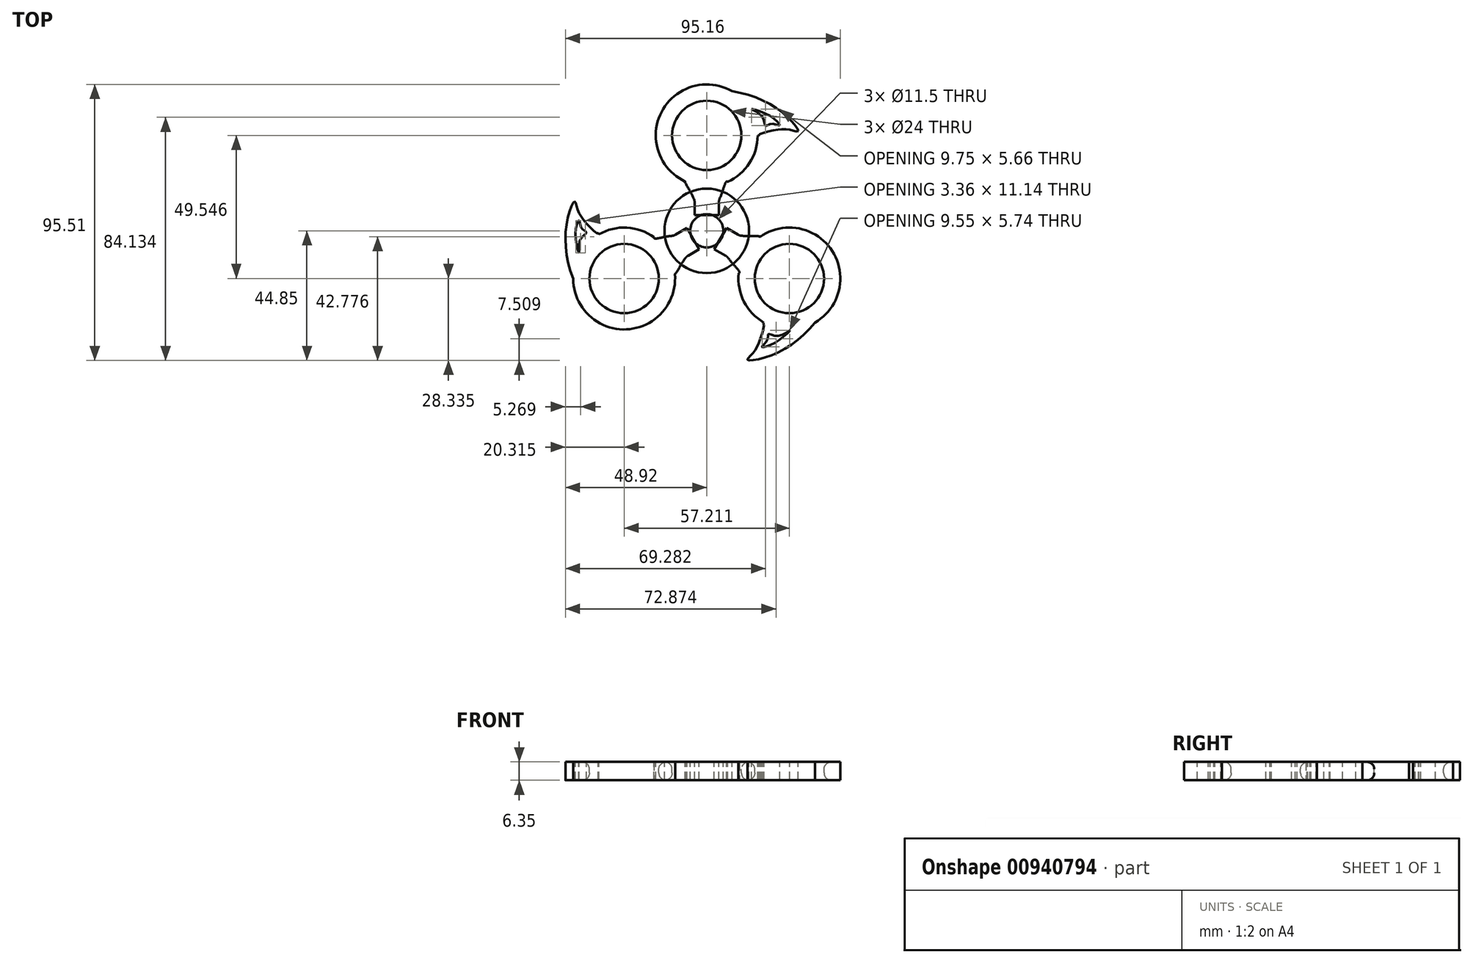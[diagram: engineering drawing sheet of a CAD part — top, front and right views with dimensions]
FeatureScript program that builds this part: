
annotation { "Feature Type Name" : "Feature", "Feature Type Description" : "" }
export const myFeature = defineFeature(function(context is Context, id is Id, definition is map)
    precondition{}
    {
        {
            var Q0;
            Q0=qCreatedBy(makeId("Top.planeOp"),FACE);
            var sketch = newSketch(context, id + "F0", { "sketchPlane" : qUnion([Q0])});
            skCircle(sketch, "E0", {"center": v(0, 0) * mm, "radius": 14.63 * mm});
            skCircle(sketch, "E1", {"center": v(0, 0) * mm, "radius": 5.75 * mm});
            skSolve(sketch);
        }
        {
            var Q0;
            Q0=qCreatedBy(makeId("Top.planeOp"),FACE);
            var sketch = newSketch(context, id + "F1", { "sketchPlane" : qUnion([Q0])});
            skCircle(sketch, "E2", {"center": v(0, 33.03) * mm, "radius": 17.63 * mm});
            skLineSegment(sketch, "E3", {"start": v(0, 0) * mm, "end": v(0, 33.03) * mm});
            skLineSegment(sketch, "E4", {"start": v(4.23, 5.44) * mm, "end": v(4.23, 10.03) * mm});
            skFitSpline(sketch, "E5", {"points": [v(4.23, 10.68) * mm, v(5.48, 13.75) * mm, v(6.36, 16.35) * mm, v(7.2, 16.93) * mm], "startDerivative": vector(2.65, 5.53) * mm, "endDerivative": vector(4.3, -5.28) * mm});
            skLineSegment(sketch, "E6.MirrorCS", {"start": v(-4.23, 5.44) * mm, "end": v(-4.23, 9.98) * mm});
            skPoint(sketch, "E7.orphan", {"position": v(4.23, 15.91) * mm});
            skFitSpline(sketch, "E8", {"points": [v(-4.23, 10.68) * mm, v(-5.95, 13.99) * mm, v(-7.53, 16.96) * mm, v(-7.4, 16.89) * mm], "startDerivative": vector(-3.15, 6.3) * mm, "endDerivative": vector(4.2, -6.48) * mm});
            skPoint(sketch, "E9.trimOffspring.end.orphan", {"position": v(-4.23, 15.91) * mm});
            skCircle(sketch, "E10", {"center": v(0, 33.03) * mm, "radius": 12 * mm});
            skArc(sketch, "E11.filletArc", {"start": v(-4.23, 9.98) * mm, "mid": v(-4.3, 10.66) * mm, "end": v(-4.54, 11.3) * mm});
            skArc(sketch, "E12.filletArc", {"start": v(4.49, 11.24) * mm, "mid": v(4.3, 10.65) * mm, "end": v(4.23, 10.03) * mm});
            skLineSegment(sketch, "E13", {"start": v(-4.23, 5.44) * mm, "end": v(4.23, 5.44) * mm});
            skPoint(sketch, "E14.oppositeSnap0", {"position": v(4.23, 7.74) * mm});
            skFitSpline(sketch, "E15", {"points": [v(15.49, 42.12) * mm, v(19.16, 39.55) * mm, v(20.33, 36.37) * mm, v(22.34, 37.04) * mm, v(25.18, 36.54) * mm, v(22, 39.72) * mm, v(15.49, 42.12) * mm]});
            skLineSegment(sketch, "E16", {"start": v(-7.4, 16.89) * mm, "end": v(-7.45, 17.05) * mm});
            skFitSpline(sketch, "E17", {"points": [v(6.04, 48.65) * mm, v(26.25, 40.87) * mm, v(31.56, 34.5) * mm, v(28.73, 35.02) * mm, v(22.7, 34.66) * mm, v(18.06, 32.99) * mm, v(20.32, 32.14) * mm], "startDerivative": vector(79.19, -6.9) * mm, "endDerivative": vector(8.4, -3.4) * mm});
            skLineSegment(sketch, "E18", {"start": v(18.06, 32.99) * mm, "end": v(17.63, 32.99) * mm});
            skSolve(sketch);
        }
        {
            var Q0;
            Q0=makeQuery(id+"F0.imprint","IMPRINT",FACE,{"disambiguationData":[TD([[makeQuery(id+"F0.imprint","IMPRINT",EDGE,{"derivedFrom":sQuery(id+"F0.wireOp",EDGE,"E0")}),1.0]])]});
            var Q1;
            {var subQ0=sQuery(id+"F1.wireOp",EDGE,"E6.MirrorCS");Q1=makeQuery(id+"F1.imprint","IMPRINT",FACE,{"disambiguationData":[TD([[makeQuery(id+"F1.imprint","IMPRINT",EDGE,{"derivedFrom":subQ0}),-1.0]])]});}
            var Q2;
            {var subQ4=sQuery(id+"F1.wireOp",EDGE,"E4");Q2=makeQuery(id+"F1.imprint","IMPRINT",FACE,{"disambiguationData":[TD([[makeQuery(id+"F1.imprint","IMPRINT",EDGE,{"derivedFrom":subQ4}),1.0]])]});}
            var Q3;
            Q3=makeQuery(id+"F1.imprint","IMPRINT",FACE,{"disambiguationData":[TD([[makeQuery(id+"F1.imprint","IMPRINT",EDGE,{"derivedFrom":sQuery(id+"F1.wireOp",EDGE,"E10")}),-1.0]])]});
            var Q4;
            {var subQ0=sQuery(id+"F1.wireOp",EDGE,"0489ace8-70b7-4bd0-9044-f4604df46fbd");var subQ1=sQuery(id+"F1.wireOp",EDGE,"E2");var subQ2=makeQuery(id+"F1.imprint","INTERSECT",VERTEX,{"disambiguationData":[OD(1.0)],"derivedFrom":[subQ1,subQ0]});Q4=makeQuery(id+"F1.imprint","IMPRINT",FACE,{"disambiguationData":[TD([[makeQuery(id+"F1.imprint","IMPRINT",EDGE,{"disambiguationData":[TD([[subQ2,1.0]])],"derivedFrom":subQ1}),-1.0]])]});}
            var Q5;
            Q5=makeQuery(id+"F1.imprint","IMPRINT",FACE,{"disambiguationData":[TD([[makeQuery(id+"F1.imprint","IMPRINT",EDGE,{"derivedFrom":sQuery(id+"F1.wireOp",EDGE,"E15")}),-1.0]])]});
            extrude(context, id + "F2", {"entities" : qUnion([Q0, Q1, Q2, Q3, Q4, Q5]), "oppositeDirection" : true, "depth" : 6.35 * mm, "offsetDistance" : 25.4 * mm});
        }
        {
            var Q0;
            Q0=makeQuery(id+"F2.opExtrude","CAP_EDGE",EDGE,{"disambiguationData":[OSD([sQuery(id+"F1.wireOp",EDGE,"E10")])],"isStart":true});
            fillet(context, id + "F3", {"entities" : qUnion([Q0]), "radius" : 2.54 * mm, "tangentPropagation" : true, "allowEdgeOverflow" : false});
        }
        {
            var Q0;
            Q0=makeQuery(id+"F2.opExtrude","CAP_EDGE",EDGE,{"disambiguationData":[OSD([sQuery(id+"F1.wireOp",EDGE,"E10")])],"isStart":false});
            fillet(context, id + "F4", {"entities" : qUnion([Q0]), "radius" : 2.54 * mm, "tangentPropagation" : true, "allowEdgeOverflow" : false});
        }
        {
            var Q0;
            Q0=makeQuery(id+"F2.opExtrude","SWEPT_BODY",BODY,{"disambiguationData":[OSD([sQuery(id+"F1.wireOp",EDGE,"E2"),sQuery(id+"F1.wireOp",EDGE,"E4"),sQuery(id+"F1.wireOp",EDGE,"E5"),sQuery(id+"F1.wireOp",EDGE,"E6.MirrorCS"),sQuery(id+"F1.wireOp",EDGE,"E8"),sQuery(id+"F1.wireOp",EDGE,"E10"),sQuery(id+"F1.wireOp",EDGE,"E11.filletArc"),sQuery(id+"F1.wireOp",EDGE,"E12.filletArc"),sQuery(id+"F1.wireOp",EDGE,"E13")])]});
            var Q1;
            Q1=makeQuery(id+"F2.opExtrude","SWEPT_BODY",BODY,{"disambiguationData":[OSD([sQuery(id+"F0.wireOp",EDGE,"E0")])]});
            var Q2;
            Q2=sQuery(id+"F0.wireOp",EDGE,"E1");
            circularPattern(context, id + "F5", {"entities" : qUnion([Q0, Q1]), "axis" : qUnion([Q2]), "angle" : 360 * degree, "instanceCount" : 3, "equalSpace" : true});
        }
    });
